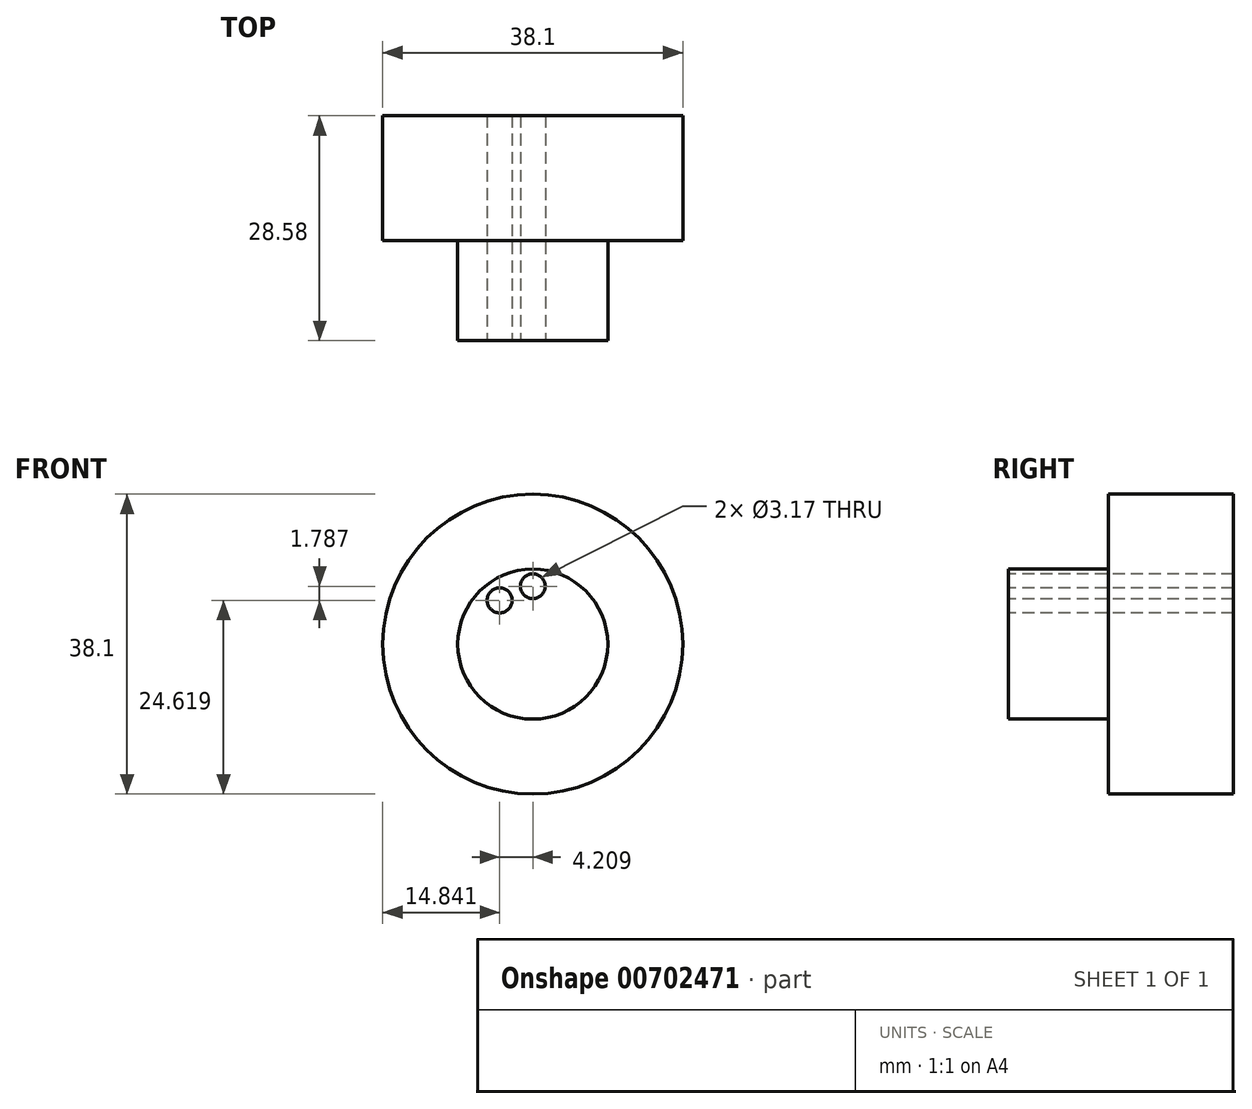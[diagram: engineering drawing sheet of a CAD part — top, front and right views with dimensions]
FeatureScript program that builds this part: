
annotation { "Feature Type Name" : "Feature", "Feature Type Description" : "" }
export const myFeature = defineFeature(function(context is Context, id is Id, definition is map)
    precondition{}
    {
        {
            var Q0;
            Q0=qCreatedBy(makeId("Front.planeOp"),FACE);
            var sketch = newSketch(context, id + "F0", { "sketchPlane" : qUnion([Q0])});
            skCircle(sketch, "E0", {"center": v(0, 0) * mm, "radius": 19.05 * mm});
            skSolve(sketch);
        }
        {
            var Q0;
            Q0 = qSketchRegion(id + "F0", true);
            extrude(context, id + "F1", {"entities" : qUnion([Q0]), "depth" : 15.88 * mm, "offsetDistance" : 25.4 * mm});
        }
        {
            var Q0;
            Q0=makeQuery(id+"F1.opExtrude","CAP_FACE",FACE,{"disambiguationData":[OSD([sQuery(id+"F0.wireOp",EDGE,"E0")])],"isStart":false});
            var sketch = newSketch(context, id + "F2", { "sketchPlane" : qUnion([Q0])});
            skCircle(sketch, "E1", {"center": v(0, 0) * mm, "radius": 9.53 * mm});
            skSolve(sketch);
        }
        {
            var Q0;
            Q0 = qSketchRegion(id + "F2", true);
            extrude(context, id + "F3", {"entities" : qUnion([Q0]), "operationType" : NewBodyOperationType.ADD, "depth" : 12.7 * mm, "offsetDistance" : 25.4 * mm});
        }
        {
            var Q0;
            Q0=makeQuery(id+"F3.opExtrude","CAP_FACE",FACE,{"disambiguationData":[OSD([sQuery(id+"F2.wireOp",EDGE,"E1")])],"isStart":false});
            var sketch = newSketch(context, id + "F4", { "sketchPlane" : qUnion([Q0])});
            skCircle(sketch, "E2", {"center": v(0, 7.36) * mm, "radius": 1.59 * mm});
            skSolve(sketch);
        }
        {
            var Q0;
            Q0 = qSketchRegion(id + "F4", true);
            extrude(context, id + "F5", {"entities" : qUnion([Q0]), "operationType" : NewBodyOperationType.REMOVE, "oppositeDirection" : true, "depth" : 50.8 * mm, "offsetDistance" : 25.4 * mm});
        }
        {
            var Q0;
            Q0=makeQuery(id+"F3.opExtrude","CAP_FACE",FACE,{"disambiguationData":[OSD([sQuery(id+"F2.wireOp",EDGE,"E1")])],"isStart":false});
            var sketch = newSketch(context, id + "F6", { "sketchPlane" : qUnion([Q0])});
            skCircle(sketch, "E3", {"center": v(-4.2, 5.57) * mm, "radius": 1.59 * mm});
            skSolve(sketch);
        }
        {
            var Q0;
            Q0 = qSketchRegion(id + "F6", true);
            extrude(context, id + "F7", {"entities" : qUnion([Q0]), "operationType" : NewBodyOperationType.REMOVE, "oppositeDirection" : true, "depth" : 50.8 * mm, "offsetDistance" : 25.4 * mm});
        }
    });
